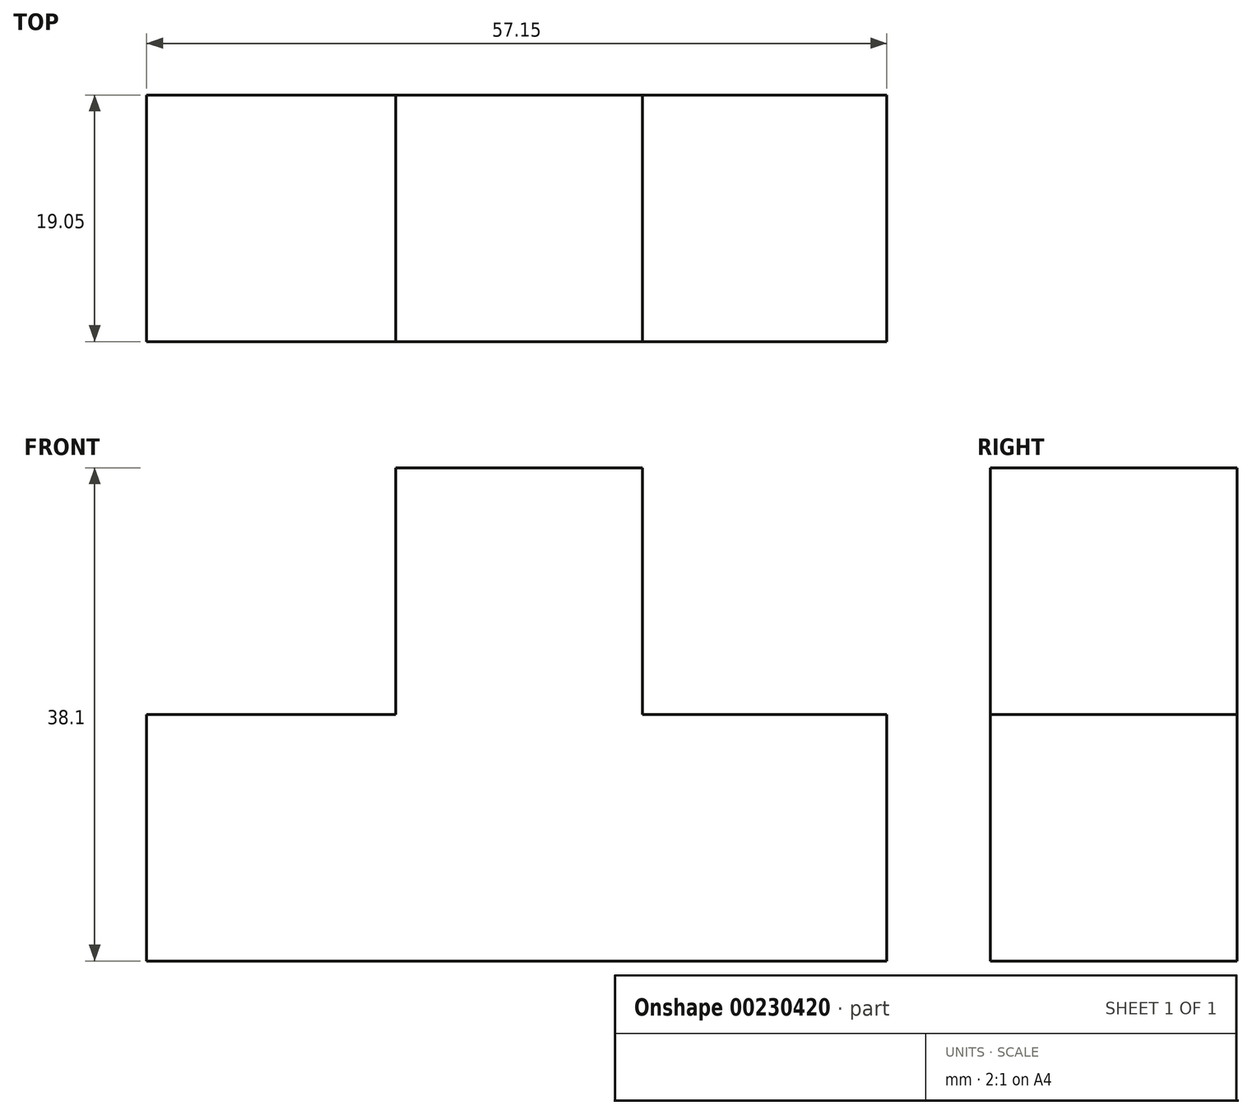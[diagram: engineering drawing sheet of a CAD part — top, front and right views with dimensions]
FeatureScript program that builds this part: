
annotation { "Feature Type Name" : "Feature", "Feature Type Description" : "" }
export const myFeature = defineFeature(function(context is Context, id is Id, definition is map)
    precondition{}
    {
        {
            var Q0;
            Q0=qCreatedBy(makeId("Front.planeOp"),FACE);
            var sketch = newSketch(context, id + "F0", { "sketchPlane" : qUnion([Q0])});
            skLineSegment(sketch, "E0.bottom", {"start": v(-94.43, 40.31) * mm, "end": v(-37.28, 40.31) * mm});
            skLineSegment(sketch, "E0.top", {"start": v(-94.43, 21.26) * mm, "end": v(-37.28, 21.26) * mm});
            skLineSegment(sketch, "E0.left", {"start": v(-94.43, 40.31) * mm, "end": v(-94.43, 21.26) * mm});
            skLineSegment(sketch, "E0.right", {"start": v(-37.28, 40.31) * mm, "end": v(-37.28, 21.26) * mm});
            skSolve(sketch);
        }
        {
            var Q0;
            Q0 = qSketchRegion(id + "F0", true);
            extrude(context, id + "F1", {"entities" : qUnion([Q0]), "depth" : 19.05 * mm});
        }
        {
            var Q0;
            Q0=makeQuery(id+"F1.opExtrude","SWEPT_FACE",FACE,{"disambiguationData":[OSD([sQuery(id+"F0.wireOp",EDGE,"E0.bottom")])]});
            var sketch = newSketch(context, id + "F2", { "sketchPlane" : qUnion([Q0])});
            skLineSegment(sketch, "E1.bottom", {"start": v(-75.19, 0) * mm, "end": v(-56.14, 0) * mm});
            skLineSegment(sketch, "E1.top", {"start": v(-75.19, -19.05) * mm, "end": v(-56.14, -19.05) * mm});
            skLineSegment(sketch, "E1.left", {"start": v(-75.19, 0) * mm, "end": v(-75.19, -19.05) * mm});
            skLineSegment(sketch, "E1.right", {"start": v(-56.14, 0) * mm, "end": v(-56.14, -19.05) * mm});
            skLineSegment(sketch, "E2.bottom", {"start": v(-56.14, -9.53) * mm, "end": v(-37.28, -9.53) * mm});
            skLineSegment(sketch, "E2.top", {"start": v(-56.14, -9.53) * mm, "end": v(-37.28, -9.53) * mm});
            skLineSegment(sketch, "E2.left", {"start": v(-56.14, -9.53) * mm, "end": v(-56.14, -9.53) * mm});
            skLineSegment(sketch, "E2.right", {"start": v(-37.28, -9.53) * mm, "end": v(-37.28, -9.53) * mm});
            skSolve(sketch);
        }
        {
            var Q0;
            {var subQ1=sQuery(id+"F2.wireOp",EDGE,"E1.bottom");Q0=makeQuery(id+"F2.imprint","IMPRINT",FACE,{"disambiguationData":[TD([[makeQuery(id+"F2.imprint","IMPRINT",EDGE,{"derivedFrom":subQ1}),-1.0]])]});}
            extrude(context, id + "F3", {"entities" : qUnion([Q0]), "operationType" : NewBodyOperationType.ADD, "depth" : 19.05 * mm});
        }
    });
